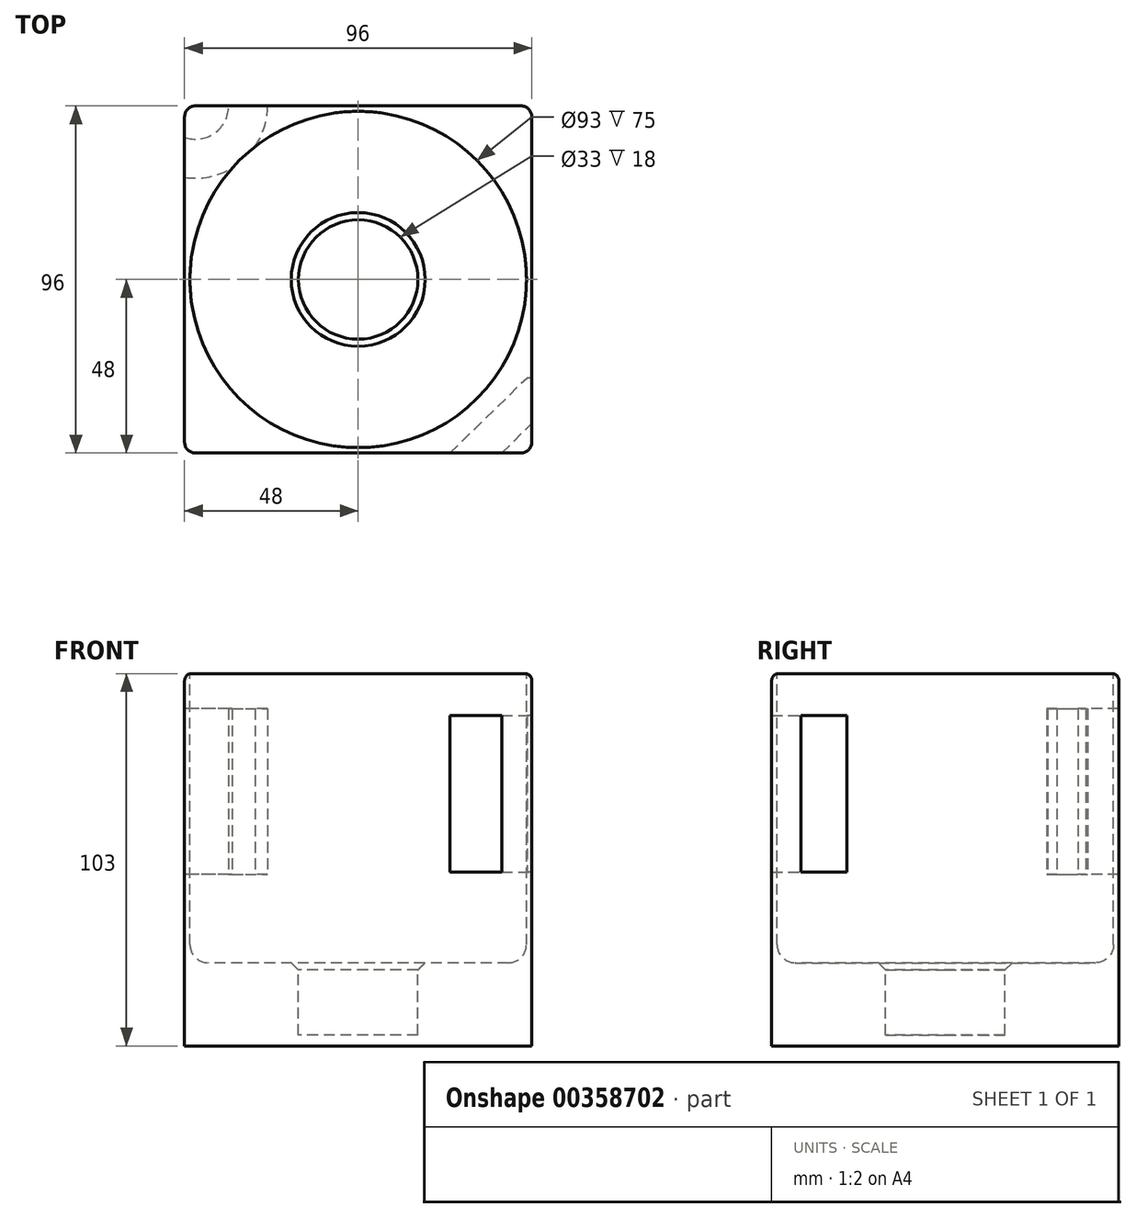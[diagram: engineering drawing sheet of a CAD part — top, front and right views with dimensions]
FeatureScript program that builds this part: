
annotation { "Feature Type Name" : "Feature", "Feature Type Description" : "" }
export const myFeature = defineFeature(function(context is Context, id is Id, definition is map)
    precondition{}
    {
        {
            var Q0;
            Q0=qCreatedBy(makeId("Top.planeOp"),FACE);
            var sketch = newSketch(context, id + "F0", { "sketchPlane" : qUnion([Q0])});
            skLineSegment(sketch, "E0.bottom", {"start": v(48, 48) * mm, "end": v(-48, 48) * mm});
            skLineSegment(sketch, "E0.top", {"start": v(48, -48) * mm, "end": v(-48, -48) * mm});
            skLineSegment(sketch, "E0.left", {"start": v(48, 48) * mm, "end": v(48, -48) * mm});
            skLineSegment(sketch, "E0.right", {"start": v(-48, 48) * mm, "end": v(-48, -48) * mm});
            skPoint(sketch, "E0.middle", {"position": v(0, 0) * mm});
            skSolve(sketch);
        }
        {
            var Q0;
            Q0=makeQuery(id+"F0.imprint","IMPRINT",FACE,{"disambiguationData":[TD([[makeQuery(id+"F0.imprint","IMPRINT",EDGE,{"derivedFrom":sQuery(id+"F0.wireOp",EDGE,"E0.bottom")}),1.0]])]});
            extrude(context, id + "F1", {"entities" : qUnion([Q0]), "depth" : 103 * mm});
        }
        {
            var Q0;
            Q0=makeQuery(id+"F1.opExtrude","CAP_FACE",FACE,{"disambiguationData":[OSD([sQuery(id+"F0.wireOp",EDGE,"E0.bottom"),sQuery(id+"F0.wireOp",EDGE,"E0.top"),sQuery(id+"F0.wireOp",EDGE,"E0.left"),sQuery(id+"F0.wireOp",EDGE,"E0.right")])],"isStart":false});
            var sketch = newSketch(context, id + "F2", { "sketchPlane" : qUnion([Q0])});
            skCircle(sketch, "E1", {"center": v(0, 0) * mm, "radius": 16.5 * mm});
            skSolve(sketch);
        }
        {
            var Q0;
            Q0 = qSketchRegion(id + "F2", true);
            extrude(context, id + "F3", {"entities" : qUnion([Q0]), "operationType" : NewBodyOperationType.REMOVE, "oppositeDirection" : true, "depth" : 100 * mm});
        }
        {
            var Q0;
            Q0=makeQuery(id+"F1.opExtrude","CAP_FACE",FACE,{"disambiguationData":[OSD([sQuery(id+"F0.wireOp",EDGE,"E0.bottom"),sQuery(id+"F0.wireOp",EDGE,"E0.top"),sQuery(id+"F0.wireOp",EDGE,"E0.left"),sQuery(id+"F0.wireOp",EDGE,"E0.right")])],"isStart":false});
            var sketch = newSketch(context, id + "F4", { "sketchPlane" : qUnion([Q0])});
            skCircle(sketch, "E2", {"center": v(0, 0) * mm, "radius": 46.5 * mm});
            skSolve(sketch);
        }
        {
            var Q0;
            Q0 = qSketchRegion(id + "F4", true);
            extrude(context, id + "F5", {"entities" : qUnion([Q0]), "operationType" : NewBodyOperationType.REMOVE, "oppositeDirection" : true, "depth" : 80 * mm});
        }
        {
            var Q0;
            Q0=makeQuery(id+"F1.opExtrude","CAP_EDGE",EDGE,{"disambiguationData":[OSD([sQuery(id+"F0.wireOp",EDGE,"E0.bottom")])],"isStart":false});
            var Q1;
            Q1=makeQuery(id+"F1.opExtrude","CAP_EDGE",EDGE,{"disambiguationData":[OSD([sQuery(id+"F0.wireOp",EDGE,"E0.left")])],"isStart":false});
            var Q2;
            Q2=makeQuery(id+"F1.opExtrude","CAP_EDGE",EDGE,{"disambiguationData":[OSD([sQuery(id+"F0.wireOp",EDGE,"E0.top")])],"isStart":false});
            var Q3;
            Q3=makeQuery(id+"F1.opExtrude","CAP_EDGE",EDGE,{"disambiguationData":[OSD([sQuery(id+"F0.wireOp",EDGE,"E0.right")])],"isStart":false});
            fillet(context, id + "F6", {"entities" : qUnion([Q0, Q1, Q2, Q3]), "radius" : 2 * mm, "tangentPropagation" : true, "allowEdgeOverflow" : false});
        }
        {
            var Q0;
            Q0=makeQuery(id+"F1.opExtrude","SWEPT_EDGE",EDGE,{"disambiguationData":[OSD([sQuery(id+"F0.wireOp",EDGE,"E0.top"),sQuery(id+"F0.wireOp",EDGE,"E0.left")])]});
            var Q1;
            Q1=makeQuery(id+"F1.opExtrude","SWEPT_EDGE",EDGE,{"disambiguationData":[OSD([sQuery(id+"F0.wireOp",EDGE,"E0.top"),sQuery(id+"F0.wireOp",EDGE,"E0.right")])]});
            var Q2;
            Q2=makeQuery(id+"F1.opExtrude","SWEPT_EDGE",EDGE,{"disambiguationData":[OSD([sQuery(id+"F0.wireOp",EDGE,"E0.bottom"),sQuery(id+"F0.wireOp",EDGE,"E0.right")])]});
            var Q3;
            Q3=makeQuery(id+"F1.opExtrude","SWEPT_EDGE",EDGE,{"disambiguationData":[OSD([sQuery(id+"F0.wireOp",EDGE,"E0.bottom"),sQuery(id+"F0.wireOp",EDGE,"E0.left")])]});
            fillet(context, id + "F7", {"entities" : qUnion([Q0, Q1, Q2, Q3]), "radius" : 3 * mm, "tangentPropagation" : true, "allowEdgeOverflow" : false});
        }
        {
            var Q0;
            Q0=makeQuery(id+"F1.opExtrude","SWEPT_FACE",FACE,{"disambiguationData":[OSD([sQuery(id+"F0.wireOp",EDGE,"E0.top")])]});
            var sketch = newSketch(context, id + "F8", { "sketchPlane" : qUnion([Q0])});
            skLineSegment(sketch, "E3.bottom", {"start": v(39.66, 91.41) * mm, "end": v(25.34, 91.41) * mm});
            skLineSegment(sketch, "E3.top", {"start": v(39.66, 48.13) * mm, "end": v(25.34, 48.13) * mm});
            skLineSegment(sketch, "E3.left", {"start": v(39.66, 91.41) * mm, "end": v(39.66, 48.13) * mm});
            skLineSegment(sketch, "E3.right", {"start": v(25.34, 91.41) * mm, "end": v(25.34, 48.13) * mm});
            skSolve(sketch);
        }
        {
            var Q0;
            Q0=makeQuery(id+"F5.boolean.opBoolean","INTERSECT",EDGE,{"derivedFrom":[makeQuery(id+"F3.boolean.opBoolean","COPY",FACE,{"derivedFrom":makeQuery(id+"F3.opExtrude","SWEPT_FACE",FACE,{"disambiguationData":[OSD([sQuery(id+"F2.wireOp",EDGE,"E1")])]})}),makeQuery(id+"F5.opExtrude","CAP_FACE",FACE,{"disambiguationData":[OSD([sQuery(id+"F4.wireOp",EDGE,"E2")])],"isStart":false})]});
            chamfer(context, id + "F9", {"entities" : qUnion([Q0]), "width" : 2 * mm, "tangentPropagation" : true});
        }
        {
            var Q0;
            Q0=makeQuery(id+"F5.boolean.opBoolean","COPY",FACE,{"derivedFrom":makeQuery(id+"F5.opExtrude","CAP_FACE",FACE,{"disambiguationData":[OSD([sQuery(id+"F4.wireOp",EDGE,"E2")])],"isStart":false})});
            var sketch = newSketch(context, id + "F10", { "sketchPlane" : qUnion([Q0])});
            skLineSegment(sketch, "E4", {"start": v(27.12, -47.92) * mm, "end": v(48.42, -27.12) * mm});
            skSolve(sketch);
        }
        {
            var Q0;
            Q0=makeQuery(id+"F8.imprint","IMPRINT",FACE,{"disambiguationData":[TD([[makeQuery(id+"F8.imprint","IMPRINT",EDGE,{"derivedFrom":sQuery(id+"F8.wireOp",EDGE,"E3.bottom")}),1.0]])]});
            var Q1;
            Q1=sQuery(id+"F10.wireOp",EDGE,"E4");
            sweep(context, id + "F11", {"operationType" : NewBodyOperationType.REMOVE, "profiles" : qUnion([Q0]), "path" : qUnion([Q1])});
        }
        {
            var Q0;
            Q0=makeQuery(id+"F5.boolean.opBoolean","COPY",EDGE,{"derivedFrom":makeQuery(id+"F5.opExtrude","CAP_EDGE",EDGE,{"disambiguationData":[OSD([sQuery(id+"F4.wireOp",EDGE,"E2")])],"isStart":false})});
            fillet(context, id + "F12", {"entities" : qUnion([Q0]), "radius" : 5 * mm, "tangentPropagation" : true, "allowEdgeOverflow" : false});
        }
        {
            var Q0;
            Q0=makeQuery(id+"F1.opExtrude","SWEPT_FACE",FACE,{"disambiguationData":[OSD([sQuery(id+"F0.wireOp",EDGE,"E0.right")])]});
            var sketch = newSketch(context, id + "F13", { "sketchPlane" : qUnion([Q0])});
            skLineSegment(sketch, "E5.bottom", {"start": v(-39.32, 93.25) * mm, "end": v(-28.27, 93.25) * mm});
            skLineSegment(sketch, "E5.top", {"start": v(-39.32, 47.42) * mm, "end": v(-28.27, 47.42) * mm});
            skLineSegment(sketch, "E5.left", {"start": v(-39.32, 93.25) * mm, "end": v(-39.32, 47.42) * mm});
            skLineSegment(sketch, "E5.right", {"start": v(-28.27, 93.25) * mm, "end": v(-28.27, 47.42) * mm});
            skSolve(sketch);
        }
        {
            var Q0;
            Q0 = qSketchRegion(id + "F13", true);
            var Q1;
            {var subQ0=sQuery(id+"F0.wireOp",EDGE,"E0.bottom");Q1=makeQuery(id+"F7.opFillet","BLEND_EDGE",EDGE,{"blendedFrom":[makeQuery(id+"F1.opExtrude","SWEPT_EDGE",EDGE,{"disambiguationData":[OSD([subQ0,sQuery(id+"F0.wireOp",EDGE,"E0.right")])]}),makeQuery(id+"F1.opExtrude","SWEPT_FACE",FACE,{"disambiguationData":[OSD([subQ0])]})],"blendedInto":[makeQuery(id+"F1.opExtrude","SWEPT_FACE",FACE,{"disambiguationData":[OSD([subQ0])]})]});}
            revolve(context, id + "F14", {"operationType" : NewBodyOperationType.REMOVE, "entities" : qUnion([Q0]), "axis" : qUnion([Q1]), "revolveType" : RevolveType.FULL, "oppositeDirection" : true});
        }
    });
